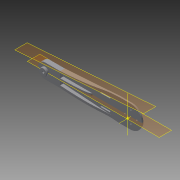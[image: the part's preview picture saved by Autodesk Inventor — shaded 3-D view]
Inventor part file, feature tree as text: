
AUTODESK INVENTOR PART (.ipt)
format: ipt  version: 2015 (Build 190159000, 159)  size: 187,904 bytes
history: native  units: mm
features: sketch x7, extrude x5, other x3, plane x2, rib x2, mirror x2, pattern_circular x1, chamfer x1, hole x1
ambient origin geometry x8: Origin, YZ Plane, XZ Plane, XY Plane, X Axis, Y Axis, Z Axis, Center Point
bodies: Body1 (feature_tree)
feature tree (24):
  extrude  "Extrusion2"  Depth=20.0mm
  plane  "Work Plane1"
  other  "Work Point1"
  extrude  "Extrusion4"  Depth=15.0mm
  other  "Work Axis2"
  pattern_circular  "Circular Pattern1"  Count=11  [1 undecoded]
  extrude  "Extrusion5"  Depth=8.0mm
  plane  "Work Plane3"
  rib  "Rib1"
  mirror  "Mirror1"
  extrude  "Extrusion6"  Depth=10.0mm TaperAngle=0.0deg
  mirror  "Mirror2"
  rib  "Rib2"
  extrude  "Extrusion7"  Depth=4.2mm TaperAngle=0.0deg
  chamfer  "Chamfer2"  Distance=50.0mm
  hole  "Hole2"  [1 undecoded]
  sketch  "Sketch2"  dims[d6=9.75mm d7=20.0mm]
  other  "Work Axis1"
  sketch  "Sketch6"  dims[d8=15.0mm d9=15.0mm d10=110.0mm]
  sketch  "Sketch7"  dims[d11=6.2mm d12=0.0mm d28=8.0mm]
  sketch  "Sketch9"  dims[d29=2.1mm d30=10.0mm d31=0.0mm]
  sketch  "Sketch10"  dims[d32=40.0mm d33=360.0deg d35=4.2mm d36=0.0mm]
  sketch  "Sketch11"  dims[d38=1.0mm]
  sketch  "Sketch12"  dims[d39=3.0mm d40=0.0mm d41=0.0mm d42=1.0mm d43=1.0mm d44=50.0mm d45=12.0mm d46=0.8mm d47=8.0mm d48=10.0mm d49=0.0mm d50=1.0mm d51=3.0mm d52=0.0mm d53=0.0mm d54=1.0mm d55=1.0mm d56=9.7mm d57=2.8mm d58=0.0mm d59=0.5mm d60=2.0mm d61=45.0deg d62=10.0mm d63=10.0mm d64=3.1mm d65=6.0mm d66=4.0mm d67=2.0mm d68=90.0deg d69=8.0mm d70=20.594885mm]
note: 2 required parameter values undecoded (feature->parameter linkage not recoverable at this tier; creation-order binding heuristic only, values carry confidence <= 0.55)
